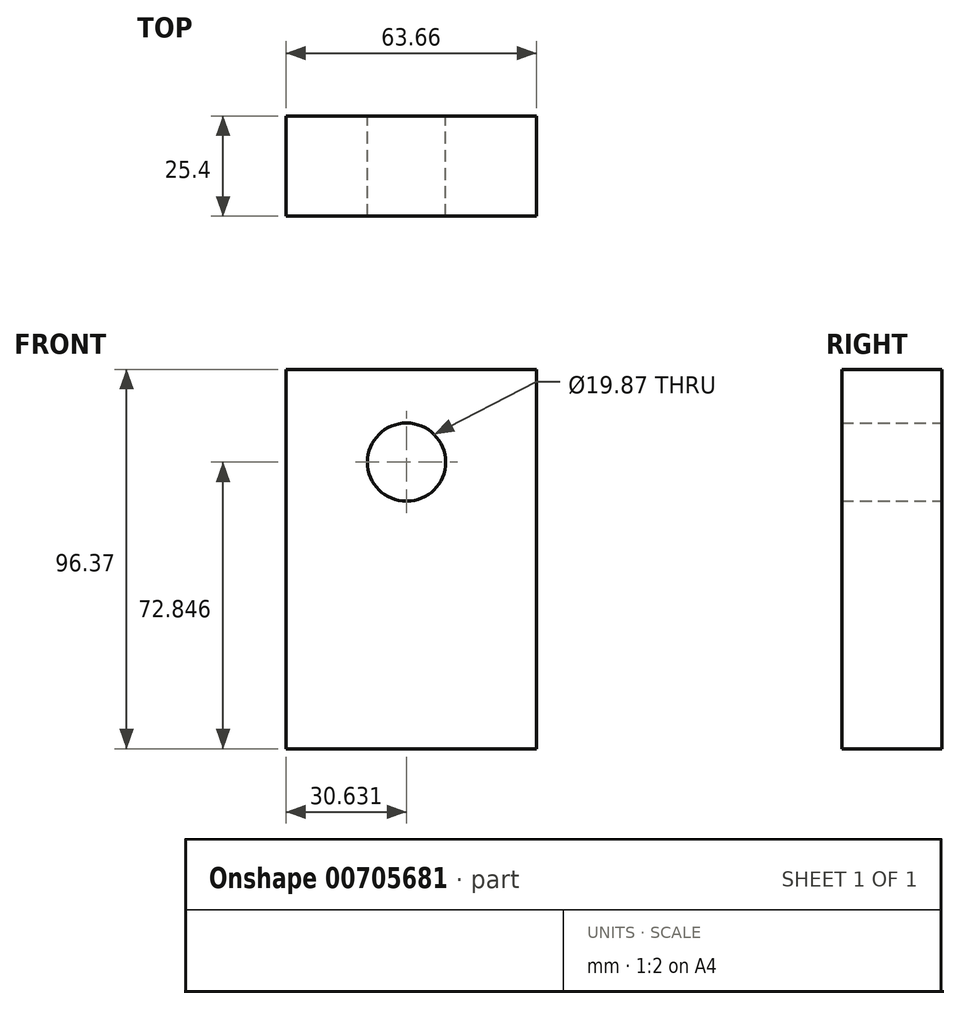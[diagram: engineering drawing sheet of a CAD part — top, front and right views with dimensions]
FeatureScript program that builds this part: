
annotation { "Feature Type Name" : "Feature", "Feature Type Description" : "" }
export const myFeature = defineFeature(function(context is Context, id is Id, definition is map)
    precondition{}
    {
        {
            var Q0;
            Q0=qCreatedBy(makeId("Front.planeOp"),FACE);
            var sketch = newSketch(context, id + "F0", { "sketchPlane" : qUnion([Q0])});
            skLineSegment(sketch, "E0.bottom", {"start": v(-36.77, -48.92) * mm, "end": v(26.89, -48.92) * mm});
            skLineSegment(sketch, "E0.top", {"start": v(-36.77, 47.45) * mm, "end": v(26.89, 47.45) * mm});
            skLineSegment(sketch, "E0.left", {"start": v(-36.77, -48.92) * mm, "end": v(-36.77, 47.45) * mm});
            skLineSegment(sketch, "E0.right", {"start": v(26.89, -48.92) * mm, "end": v(26.89, 47.45) * mm});
            skCircle(sketch, "E1", {"center": v(-6.14, 23.93) * mm, "radius": 9.93 * mm});
            skSolve(sketch);
        }
        {
            var Q0;
            Q0 = qSketchRegion(id + "F0", true);
            extrude(context, id + "F1", {"entities" : qUnion([Q0]), "depth" : 25.4 * mm, "offsetDistance" : 25.4 * mm});
        }
    });
